# Revit family: ВУТ_ВУЕ ГБ_Е_Eng
name_source: partatom
category: Mechanical Equipment
units: mm (PartAtom-declared; Revit-internal decimal feet)

## family parameters
Always vertical = Yes
Classification = None
Cut with Voids When Loaded = No
Part Type = Normal
Room Calculation Point = No
Round Connector Dimension = Use Diameter
Shared = No
Work Plane-Based = No

## types (12) — shared parameters
00_20_Manufacturer = Vents
00_20_Name = Air handling units with heat recovery
Casing Material = Steel, galvanized
Filter = G4+F7/G4
Frequency = 0 Hz
Load Classification = HVAC
Maintenance zone material = <By Category>
Manufacturer = Vents
Number of Fase = 1
URL = https://ventilation-system.com
Voltage = 230 V
zero-valued in all types: Default Elevation

## per-type parameters (varying)
| type | Amperage | Apparent Load | B | B1 | B2 | D | Diameter | Direction | Dy | H | H1 | H2 | H3 | Height | L | L1 | Leg | Length | Maximum Air Flow | Power | Sound pressure level at 3 m distance | Weight | Width | l1 |
| VUE 300 HB EС А21 | 1 A | 322 VA | 566 mm  [stored 1.85696 ft] | 379 mm  [stored 1.24344 ft] | 189 mm  [stored 0.620079 ft] | 160 mm  [stored 0.524934 ft] | 160 mm  [stored 0.524934 ft] | 462 mm | 155 mm  [stored 0.50853 ft] | 479 mm  [stored 1.57152 ft] | 311 mm  [stored 1.02034 ft] | 118 mm | 499 mm  [stored 1.63714 ft] | 499 mm  [stored 1.63714 ft] | 1083 mm  [stored 3.55315 ft] | 1180 mm  [stored 3.87139 ft] | 72 mm | 1180 mm  [stored 3.87139 ft] | 380.0 m³/h | 182 W | 24 dBA | 63.10 kg | 566 mm  [stored 1.85696 ft] | 590 mm  [stored 1.9357 ft] |
| VUE 400 HB EС А21 | 2 A | 483 VA | 682 mm | 465 mm  [stored 1.52559 ft] | 217 mm  [stored 0.711942 ft] | 200 mm  [stored 0.656168 ft] | 200 mm  [stored 0.656168 ft] | 467 mm  [stored 1.53215 ft] | 195 mm  [stored 0.639764 ft] | 504 mm  [stored 1.65354 ft] | 342 mm  [stored 1.12205 ft] | 141 mm | 524 mm  [stored 1.71916 ft] | 524 mm  [stored 1.71916 ft] | 1094 mm | 1191 mm | 73 mm | 1191 mm | 540.0 m³/h | 289 W | 27 dBA | 74.80 kg | 682 mm | 596 mm |
| VUE 700 HB EС А21 | 2 A | 552 VA | 866 mm | 570 mm  [stored 1.87008 ft] | 296 mm  [stored 0.971129 ft] | 250 mm  [stored 0.82021 ft] | 250 mm  [stored 0.82021 ft] | 561 mm | 245 mm  [stored 0.803806 ft] | 601 mm  [stored 1.97178 ft] | 400 mm  [stored 1.31234 ft] | 166 mm  [stored 0.544619 ft] | 621 mm  [stored 2.0374 ft] | 621 mm  [stored 2.0374 ft] | 1282 mm | 1379 mm | 85 mm | 1379 mm | 830.0 m³/h | 336 W | 31 dBA | 107.00 kg | 866 mm | 690 mm |
| VUE 300 HBE EС А21 | 14 A | 3128 VA | 566 mm  [stored 1.85696 ft] | 379 mm  [stored 1.24344 ft] | 189 mm  [stored 0.620079 ft] | 160 mm  [stored 0.524934 ft] | 160 mm  [stored 0.524934 ft] | 462 mm | 155 mm  [stored 0.50853 ft] | 479 mm  [stored 1.57152 ft] | 311 mm  [stored 1.02034 ft] | 118 mm | 499 mm  [stored 1.63714 ft] | 499 mm  [stored 1.63714 ft] | 1083 mm  [stored 3.55315 ft] | 1180 mm  [stored 3.87139 ft] | 72 mm | 1180 mm  [stored 3.87139 ft] | 380.0 m³/h | 2982 W | 24 dBA | 64.30 kg | 566 mm  [stored 1.85696 ft] | 590 mm  [stored 1.9357 ft] |
| VUE 400 HBE EС А21 | 14 A | 3289 VA | 682 mm | 465 mm  [stored 1.52559 ft] | 217 mm  [stored 0.711942 ft] | 200 mm  [stored 0.656168 ft] | 200 mm  [stored 0.656168 ft] | 467 mm  [stored 1.53215 ft] | 195 mm  [stored 0.639764 ft] | 504 mm  [stored 1.65354 ft] | 342 mm  [stored 1.12205 ft] | 141 mm | 524 mm  [stored 1.71916 ft] | 524 mm  [stored 1.71916 ft] | 1094 mm | 1191 mm | 73 mm | 1191 mm | 540.0 m³/h | 3089 W | 27 dBA | 76.00 kg | 682 mm | 596 mm |
| VUE 700 HBE EС А21 | 18 A | 4140 VA | 866 mm | 570 mm  [stored 1.87008 ft] | 296 mm  [stored 0.971129 ft] | 250 mm  [stored 0.82021 ft] | 250 mm  [stored 0.82021 ft] | 561 mm | 245 mm  [stored 0.803806 ft] | 601 mm  [stored 1.97178 ft] | 400 mm  [stored 1.31234 ft] | 166 mm  [stored 0.544619 ft] | 621 mm  [stored 2.0374 ft] | 621 mm  [stored 2.0374 ft] | 1282 mm | 1379 mm | 85 mm | 1379 mm | 830.0 m³/h | 3936 W | 31 dBA | 108.40 kg | 866 mm | 690 mm |
| VUT 300 HB EС А21 | 1 A | 322 VA | 566 mm  [stored 1.85696 ft] | 379 mm  [stored 1.24344 ft] | 189 mm  [stored 0.620079 ft] | 160 mm  [stored 0.524934 ft] | 160 mm  [stored 0.524934 ft] | 462 mm | 155 mm  [stored 0.50853 ft] | 479 mm  [stored 1.57152 ft] | 311 mm  [stored 1.02034 ft] | 118 mm | 499 mm  [stored 1.63714 ft] | 499 mm  [stored 1.63714 ft] | 1083 mm  [stored 3.55315 ft] | 1180 mm  [stored 3.87139 ft] | 72 mm | 1180 mm  [stored 3.87139 ft] | 380.0 m³/h | 182 W | 24 dBA | 63.10 kg | 566 mm  [stored 1.85696 ft] | 590 mm  [stored 1.9357 ft] |
| VUT 300 HBE EС А21 | 14 A | 3128 VA | 566 mm  [stored 1.85696 ft] | 379 mm  [stored 1.24344 ft] | 189 mm  [stored 0.620079 ft] | 160 mm  [stored 0.524934 ft] | 160 mm  [stored 0.524934 ft] | 462 mm | 155 mm  [stored 0.50853 ft] | 479 mm  [stored 1.57152 ft] | 311 mm  [stored 1.02034 ft] | 118 mm | 499 mm  [stored 1.63714 ft] | 499 mm  [stored 1.63714 ft] | 1083 mm  [stored 3.55315 ft] | 1180 mm  [stored 3.87139 ft] | 72 mm | 1180 mm  [stored 3.87139 ft] | 380.0 m³/h | 2982 W | 24 dBA | 64.30 kg | 566 mm  [stored 1.85696 ft] | 590 mm  [stored 1.9357 ft] |
| VUT 400 HB EС А21 | 2 A | 483 VA | 682 mm | 465 mm  [stored 1.52559 ft] | 217 mm  [stored 0.711942 ft] | 200 mm  [stored 0.656168 ft] | 200 mm  [stored 0.656168 ft] | 467 mm  [stored 1.53215 ft] | 195 mm  [stored 0.639764 ft] | 504 mm  [stored 1.65354 ft] | 342 mm  [stored 1.12205 ft] | 141 mm | 524 mm  [stored 1.71916 ft] | 524 mm  [stored 1.71916 ft] | 1094 mm | 1191 mm | 73 mm | 1191 mm | 540.0 m³/h | 289 W | 27 dBA | 74.80 kg | 682 mm | 596 mm |
| VUT 400 HBE EС А21 | 14 A | 3289 VA | 682 mm | 465 mm  [stored 1.52559 ft] | 217 mm  [stored 0.711942 ft] | 200 mm  [stored 0.656168 ft] | 200 mm  [stored 0.656168 ft] | 467 mm  [stored 1.53215 ft] | 195 mm  [stored 0.639764 ft] | 504 mm  [stored 1.65354 ft] | 342 mm  [stored 1.12205 ft] | 141 mm | 524 mm  [stored 1.71916 ft] | 524 mm  [stored 1.71916 ft] | 1094 mm | 1191 mm | 73 mm | 1191 mm | 540.0 m³/h | 3089 W | 27 dBA | 76.00 kg | 682 mm | 596 mm |
| VUT 700 HB EС А21 | 2 A | 552 VA | 866 mm | 570 mm  [stored 1.87008 ft] | 296 mm  [stored 0.971129 ft] | 250 mm  [stored 0.82021 ft] | 250 mm  [stored 0.82021 ft] | 561 mm | 245 mm  [stored 0.803806 ft] | 601 mm  [stored 1.97178 ft] | 400 mm  [stored 1.31234 ft] | 166 mm  [stored 0.544619 ft] | 621 mm  [stored 2.0374 ft] | 621 mm  [stored 2.0374 ft] | 1282 mm | 1379 mm | 85 mm | 1379 mm | 830.0 m³/h | 336 W | 31 dBA | 107.00 kg | 866 mm | 690 mm |
| VUT 700 HBE EС А21 | 18 A | 4140 VA | 866 mm | 570 mm  [stored 1.87008 ft] | 296 mm  [stored 0.971129 ft] | 250 mm  [stored 0.82021 ft] | 250 mm  [stored 0.82021 ft] | 561 mm | 245 mm  [stored 0.803806 ft] | 601 mm  [stored 1.97178 ft] | 400 mm  [stored 1.31234 ft] | 166 mm  [stored 0.544619 ft] | 621 mm  [stored 2.0374 ft] | 621 mm  [stored 2.0374 ft] | 1282 mm | 1379 mm | 85 mm | 1379 mm | 830.0 m³/h | 3936 W | 31 dBA | 108.40 kg | 866 mm | 690 mm |

note: column(s) folded — value = type name in every type: 00_20_Type

note: [stored X ft] marks values corroborated as IEEE doubles in the binary element streams (Revit-internal decimal feet)
